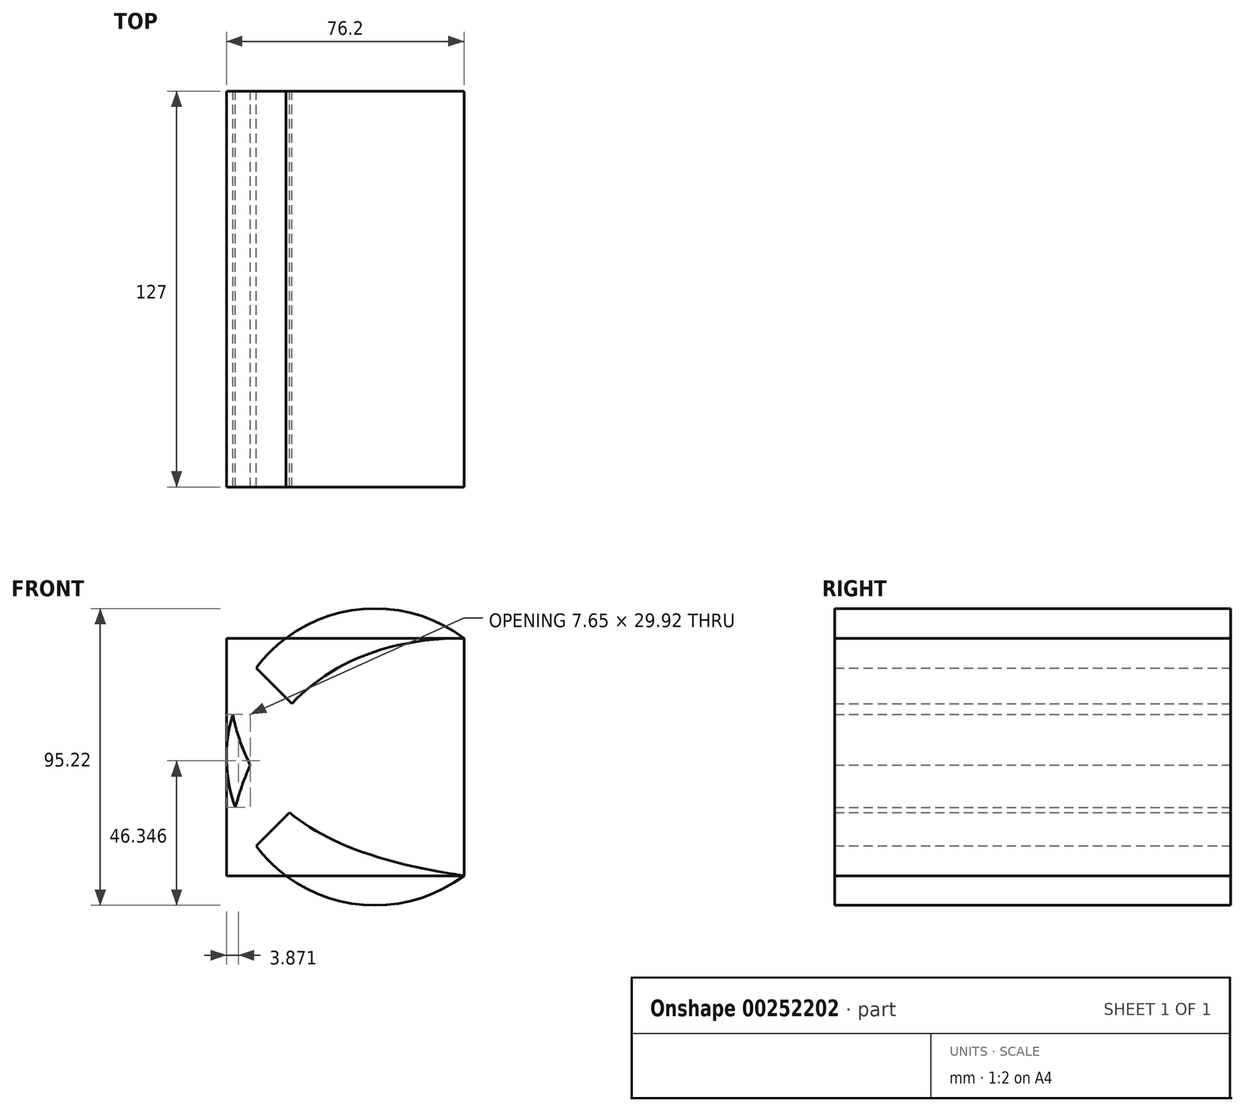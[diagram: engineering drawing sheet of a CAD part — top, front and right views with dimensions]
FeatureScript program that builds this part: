
annotation { "Feature Type Name" : "Feature", "Feature Type Description" : "" }
export const myFeature = defineFeature(function(context is Context, id is Id, definition is map)
    precondition{}
    {
        {
            var Q0;
            Q0=qCreatedBy(makeId("Front.planeOp"),FACE);
            var sketch = newSketch(context, id + "F0", { "sketchPlane" : qUnion([Q0])});
            skLineSegment(sketch, "E0.bottom", {"start": v(-38.1, 38.1) * mm, "end": v(38.1, 38.1) * mm});
            skLineSegment(sketch, "E0.top", {"start": v(-38.1, -38.1) * mm, "end": v(38.1, -38.1) * mm});
            skLineSegment(sketch, "E0.left", {"start": v(-38.1, 38.1) * mm, "end": v(-38.1, -38.1) * mm});
            skLineSegment(sketch, "E0.right", {"start": v(38.1, 38.1) * mm, "end": v(38.1, -38.1) * mm});
            skPoint(sketch, "E0.middle", {"position": v(0, 0) * mm});
            skArc(sketch, "E1", {"start": v(38.1, 38.1) * mm, "mid": v(-38.07, 0) * mm, "end": v(38.1, -38.1) * mm});
            skLineSegment(sketch, "E2", {"start": v(0, 0) * mm, "end": v(-38.1, 38.1) * mm});
            skLineSegment(sketch, "E3", {"start": v(0, 0) * mm, "end": v(-38.1, -38.1) * mm});
            skFitSpline(sketch, "E4", {"points": [v(38.1, -38.1) * mm, v(-38.1, 38.1) * mm], "startDerivative": vector(-199.97, 28.63) * mm, "endDerivative": vector(0, 114.3) * mm});
            skFitSpline(sketch, "E5", {"points": [v(38.1, 38.1) * mm, v(-38.1, -38.1) * mm], "startDerivative": vector(-171.34, 0) * mm, "endDerivative": vector(-0.9, -99.02) * mm});
            skSolve(sketch);
        }
        {
            var Q0;
            {var subQ0=sQuery(id+"F0.wireOp",EDGE,"E1");var subQ1=sQuery(id+"F0.wireOp",EDGE,"E0.bottom");var subQ3=makeQuery(id+"F0.imprint","INTERSECT",VERTEX,{"derivedFrom":[subQ1,subQ0]});Q0=makeQuery(id+"F0.imprint","IMPRINT",FACE,{"disambiguationData":[TD([[makeQuery(id+"F0.imprint","IMPRINT",EDGE,{"disambiguationData":[TD([[subQ3,-1.0]])],"derivedFrom":subQ1}),1.0]])]});}
            var Q1;
            {var subQ1=sQuery(id+"F0.wireOp",EDGE,"E0.bottom");var subQ3=sQuery(id+"F0.wireOp",EDGE,"E1");var subQ4=makeQuery(id+"F0.imprint","INTERSECT",VERTEX,{"derivedFrom":[subQ1,subQ3]});Q1=makeQuery(id+"F0.imprint","IMPRINT",FACE,{"disambiguationData":[TD([[makeQuery(id+"F0.imprint","IMPRINT",EDGE,{"disambiguationData":[TD([[subQ4,-1.0]])],"derivedFrom":subQ3}),-1.0]])]});}
            var Q2;
            {var subQ0=sQuery(id+"F0.wireOp",EDGE,"E2");var subQ1=sQuery(id+"F0.wireOp",EDGE,"E1");var subQ2=makeQuery(id+"F0.imprint","INTERSECT",VERTEX,{"derivedFrom":[subQ1,subQ0]});Q2=makeQuery(id+"F0.imprint","IMPRINT",FACE,{"disambiguationData":[TD([[makeQuery(id+"F0.imprint","IMPRINT",EDGE,{"disambiguationData":[TD([[subQ2,-1.0]])],"derivedFrom":subQ1}),-1.0]])]});}
            var Q3;
            {var subQ0=sQuery(id+"F0.wireOp",EDGE,"E0.left");Q3=makeQuery(id+"F0.imprint","IMPRINT",FACE,{"disambiguationData":[TD([[makeQuery(id+"F0.imprint","IMPRINT",EDGE,{"derivedFrom":subQ0}),1.0]])]});}
            var Q4;
            {var subQ0=sQuery(id+"F0.wireOp",EDGE,"E5");var subQ1=sQuery(id+"F0.wireOp",EDGE,"E1");var subQ2=makeQuery(id+"F0.imprint","INTERSECT",VERTEX,{"derivedFrom":[subQ1,subQ0]});Q4=makeQuery(id+"F0.imprint","IMPRINT",FACE,{"disambiguationData":[TD([[makeQuery(id+"F0.imprint","IMPRINT",EDGE,{"disambiguationData":[TD([[subQ2,-1.0]])],"derivedFrom":subQ1}),-1.0]])]});}
            var Q5;
            {var subQ1=sQuery(id+"F0.wireOp",EDGE,"E0.top");var subQ3=sQuery(id+"F0.wireOp",EDGE,"E1");var subQ4=makeQuery(id+"F0.imprint","INTERSECT",VERTEX,{"derivedFrom":[subQ1,subQ3]});Q5=makeQuery(id+"F0.imprint","IMPRINT",FACE,{"disambiguationData":[TD([[makeQuery(id+"F0.imprint","IMPRINT",EDGE,{"disambiguationData":[TD([[subQ4,1.0]])],"derivedFrom":subQ3}),-1.0]])]});}
            var Q6;
            {var subQ0=sQuery(id+"F0.wireOp",EDGE,"E1");var subQ1=sQuery(id+"F0.wireOp",EDGE,"E0.top");var subQ3=makeQuery(id+"F0.imprint","INTERSECT",VERTEX,{"derivedFrom":[subQ1,subQ0]});Q6=makeQuery(id+"F0.imprint","IMPRINT",FACE,{"disambiguationData":[TD([[makeQuery(id+"F0.imprint","IMPRINT",EDGE,{"disambiguationData":[TD([[subQ3,-1.0]])],"derivedFrom":subQ1}),-1.0]])]});}
            var Q7;
            {var subQ5=sQuery(id+"F0.wireOp",EDGE,"E0.right");Q7=makeQuery(id+"F0.imprint","IMPRINT",FACE,{"disambiguationData":[TD([[makeQuery(id+"F0.imprint","IMPRINT",EDGE,{"derivedFrom":subQ5}),-1.0]])]});}
            var Q8;
            {var subQ0=sQuery(id+"F0.wireOp",EDGE,"E2");var subQ1=sQuery(id+"F0.wireOp",EDGE,"E1");var subQ2=makeQuery(id+"F0.imprint","INTERSECT",VERTEX,{"derivedFrom":[subQ1,subQ0]});Q8=makeQuery(id+"F0.imprint","IMPRINT",FACE,{"disambiguationData":[TD([[makeQuery(id+"F0.imprint","IMPRINT",EDGE,{"disambiguationData":[TD([[subQ2,-1.0]])],"derivedFrom":subQ1}),1.0]])]});}
            var Q9;
            {var subQ0=sQuery(id+"F0.wireOp",EDGE,"E5");var subQ1=sQuery(id+"F0.wireOp",EDGE,"E1");var subQ2=makeQuery(id+"F0.imprint","INTERSECT",VERTEX,{"derivedFrom":[subQ1,subQ0]});Q9=makeQuery(id+"F0.imprint","IMPRINT",FACE,{"disambiguationData":[TD([[makeQuery(id+"F0.imprint","IMPRINT",EDGE,{"disambiguationData":[TD([[subQ2,-1.0]])],"derivedFrom":subQ1}),1.0]])]});}
            var Q10;
            {var subQ0=sQuery(id+"F0.wireOp",EDGE,"E3");var subQ1=sQuery(id+"F0.wireOp",EDGE,"E2");var subQ2=makeQuery(id+"F0.imprint","INTERSECT",VERTEX,{"derivedFrom":[subQ1,subQ0]});Q10=makeQuery(id+"F0.imprint","IMPRINT",FACE,{"disambiguationData":[TD([[makeQuery(id+"F0.imprint","IMPRINT",EDGE,{"disambiguationData":[TD([[subQ2,-1.0]])],"derivedFrom":subQ1}),1.0]])]});}
            extrude(context, id + "F1", {"entities" : qUnion([Q0, Q1, Q2, Q3, Q4, Q5, Q6, Q7, Q8, Q9, Q10]), "endBound" : BoundingType.SYMMETRIC, "depth" : 127 * mm});
        }
    });
